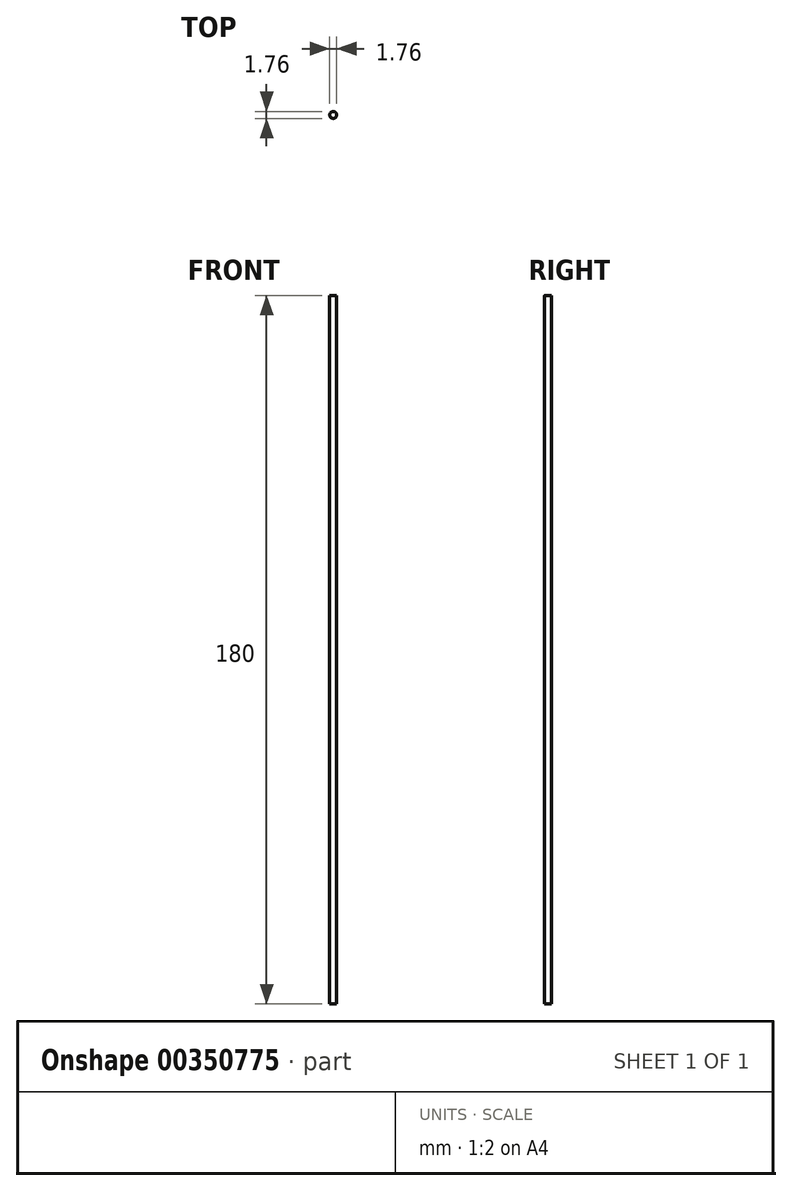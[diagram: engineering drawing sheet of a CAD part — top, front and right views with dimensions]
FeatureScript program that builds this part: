
annotation { "Feature Type Name" : "Feature", "Feature Type Description" : "" }
export const myFeature = defineFeature(function(context is Context, id is Id, definition is map)
    precondition{}
    {
        {
            var Q0;
            Q0=qCreatedBy(makeId("Top.planeOp"),FACE);
            var sketch = newSketch(context, id + "F0", { "sketchPlane" : qUnion([Q0])});
            skLineSegment(sketch, "E0.bottom", {"start": v(167.1, 194) * mm, "end": v(-167.1, 194) * mm});
            skLineSegment(sketch, "E0.top", {"start": v(167.1, -194) * mm, "end": v(-167.1, -194) * mm});
            skLineSegment(sketch, "E0.left", {"start": v(167.1, 194) * mm, "end": v(167.1, -194) * mm});
            skLineSegment(sketch, "E0.right", {"start": v(-167.1, 194) * mm, "end": v(-167.1, -194) * mm});
            skPoint(sketch, "E0.middle", {"position": v(0, 0) * mm});
            skLineSegment(sketch, "E1", {"start": v(-167.1, 194) * mm, "end": v(-167.1, 0) * mm});
            skLineSegment(sketch, "E2", {"start": v(-167.1, 0) * mm, "end": v(-167.1, -194) * mm});
            skLineSegment(sketch, "E3", {"start": v(167.1, -194) * mm, "end": v(167.1, 0) * mm});
            skLineSegment(sketch, "E4", {"start": v(167.1, 0) * mm, "end": v(167.1, 194) * mm});
            skLineSegment(sketch, "E5", {"start": v(-167.1, 0) * mm, "end": v(167.1, 0) * mm});
            skLineSegment(sketch, "E6", {"start": v(-161.1, -188) * mm, "end": v(-161.1, 189) * mm});
            skLineSegment(sketch, "E7", {"start": v(-161.1, 189) * mm, "end": v(162.1, 189) * mm});
            skLineSegment(sketch, "E8", {"start": v(162.1, 189) * mm, "end": v(162.1, -188) * mm});
            skLineSegment(sketch, "E9", {"start": v(162.1, -188) * mm, "end": v(-161.1, -188) * mm});
            skLineSegment(sketch, "E10", {"start": v(-167.1, 0) * mm, "end": v(-161.1, 0) * mm});
            skLineSegment(sketch, "E11", {"start": v(-161.1, 0) * mm, "end": v(162.1, 0) * mm});
            skLineSegment(sketch, "E12", {"start": v(162.1, 0) * mm, "end": v(167.1, 0) * mm});
            skLineSegment(sketch, "E13", {"start": v(164.6, 0) * mm, "end": v(-164.1, 0) * mm});
            skLineSegment(sketch, "E14.bottom", {"start": v(-157.1, 50) * mm, "end": v(-171.1, 50) * mm});
            skLineSegment(sketch, "E14.top", {"start": v(-157.1, -50) * mm, "end": v(-171.1, -50) * mm});
            skLineSegment(sketch, "E14.left", {"start": v(-157.1, 50) * mm, "end": v(-157.1, -50) * mm});
            skLineSegment(sketch, "E14.right", {"start": v(-171.1, 50) * mm, "end": v(-171.1, -50) * mm});
            skPoint(sketch, "E14.middle", {"position": v(-164.1, 0) * mm});
            skLineSegment(sketch, "E15.bottom", {"start": v(171.1, 50) * mm, "end": v(158.1, 50) * mm});
            skLineSegment(sketch, "E15.top", {"start": v(171.1, -50) * mm, "end": v(158.1, -50) * mm});
            skLineSegment(sketch, "E15.left", {"start": v(171.1, 50) * mm, "end": v(171.1, -50) * mm});
            skLineSegment(sketch, "E15.right", {"start": v(158.1, 50) * mm, "end": v(158.1, -50) * mm});
            skPoint(sketch, "E15.middle", {"position": v(164.6, 0) * mm});
            skLineSegment(sketch, "E16.bottom", {"start": v(158.1, 5) * mm, "end": v(162.1, 5) * mm});
            skLineSegment(sketch, "E16.top", {"start": v(158.1, -5) * mm, "end": v(162.1, -5) * mm});
            skLineSegment(sketch, "E16.left", {"start": v(158.1, 5) * mm, "end": v(158.1, -5) * mm});
            skLineSegment(sketch, "E16.right", {"start": v(162.1, 5) * mm, "end": v(162.1, -5) * mm});
            skLineSegment(sketch, "E17.bottom", {"start": v(-157.1, 5) * mm, "end": v(-161.1, 5) * mm});
            skLineSegment(sketch, "E17.top", {"start": v(-157.1, -5) * mm, "end": v(-161.1, -5) * mm});
            skLineSegment(sketch, "E17.left", {"start": v(-157.1, 5) * mm, "end": v(-157.1, -5) * mm});
            skLineSegment(sketch, "E17.right", {"start": v(-161.1, 5) * mm, "end": v(-161.1, -5) * mm});
            skSolve(sketch);
        }
        {
            var Q0;
            Q0=qCreatedBy(makeId("Front.planeOp"),FACE);
            cPlane(context, id + "F1", {"entities" : qUnion([Q0]), "cplaneType" : CPlaneType.OFFSET, "offset" : 5 * mm, "oppositeDirection" : true, "width" : 150 * mm, "height" : 150 * mm});
        }
        {
            var Q0;
            Q0=qCreatedBy(makeId("Top.planeOp"),FACE);
            cPlane(context, id + "F2", {"entities" : qUnion([Q0]), "cplaneType" : CPlaneType.OFFSET, "offset" : 70 * mm, "width" : 150 * mm, "height" : 150 * mm});
        }
        {
            var Q0;
            Q0=qCreatedBy(id+"F2.planeOp",FACE);
            var sketch = newSketch(context, id + "F3", { "sketchPlane" : qUnion([Q0])});
            skLineSegment(sketch, "E18", {"start": v(0, 0) * mm, "end": v(0, 20) * mm});
            skCircle(sketch, "E19", {"center": v(0, 20) * mm, "radius": 0.87 * mm});
            skSolve(sketch);
        }
        {
            var Q0;
            Q0=makeQuery(id+"F3.imprint","IMPRINT",FACE,{"disambiguationData":[TD([[makeQuery(id+"F3.imprint","IMPRINT",EDGE,{"derivedFrom":sQuery(id+"F3.wireOp",EDGE,"E19")}),1.0]])]});
            var Q1;
            Q1=sQuery(id+"F3.wireOp",EDGE,"E19");
            extrude(context, id + "F4", {"entities" : qUnion([Q0]), "surfaceEntities" : qUnion([Q1]), "endBound" : BoundingType.SYMMETRIC, "depth" : 180 * mm});
        }
    });
